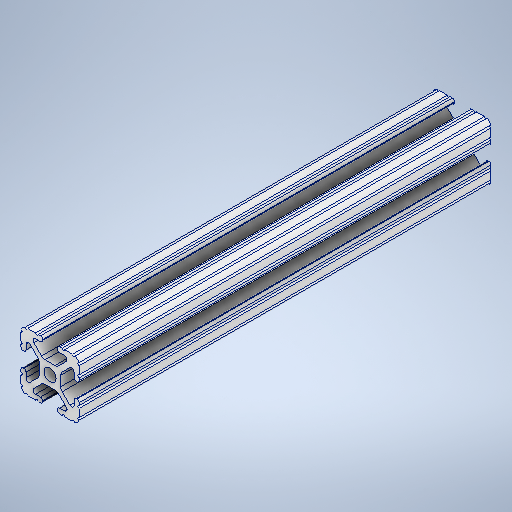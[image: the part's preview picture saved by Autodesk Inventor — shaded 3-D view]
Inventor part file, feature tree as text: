
AUTODESK INVENTOR PART (.ipt)
format: ipt  version: 2025 (Build 290162000, 162)  size: 390,144 bytes
history: native  units: mm
features: extrude x1, sketch x1, mirror x1
ambient origin geometry x8: Origin, YZ Plane, XZ Plane, XY Plane, X Axis, Y Axis, Z Axis, Center Point
bodies: Solid1 (feature_tree)
feature tree (3):
  extrude  "Extrusion1"  Depth=180.0mm
  sketch  "Sketch1"  dims[d1=0.0mm d2=0.0mm d4=180.0mm]
  mirror  "Mirror2"
